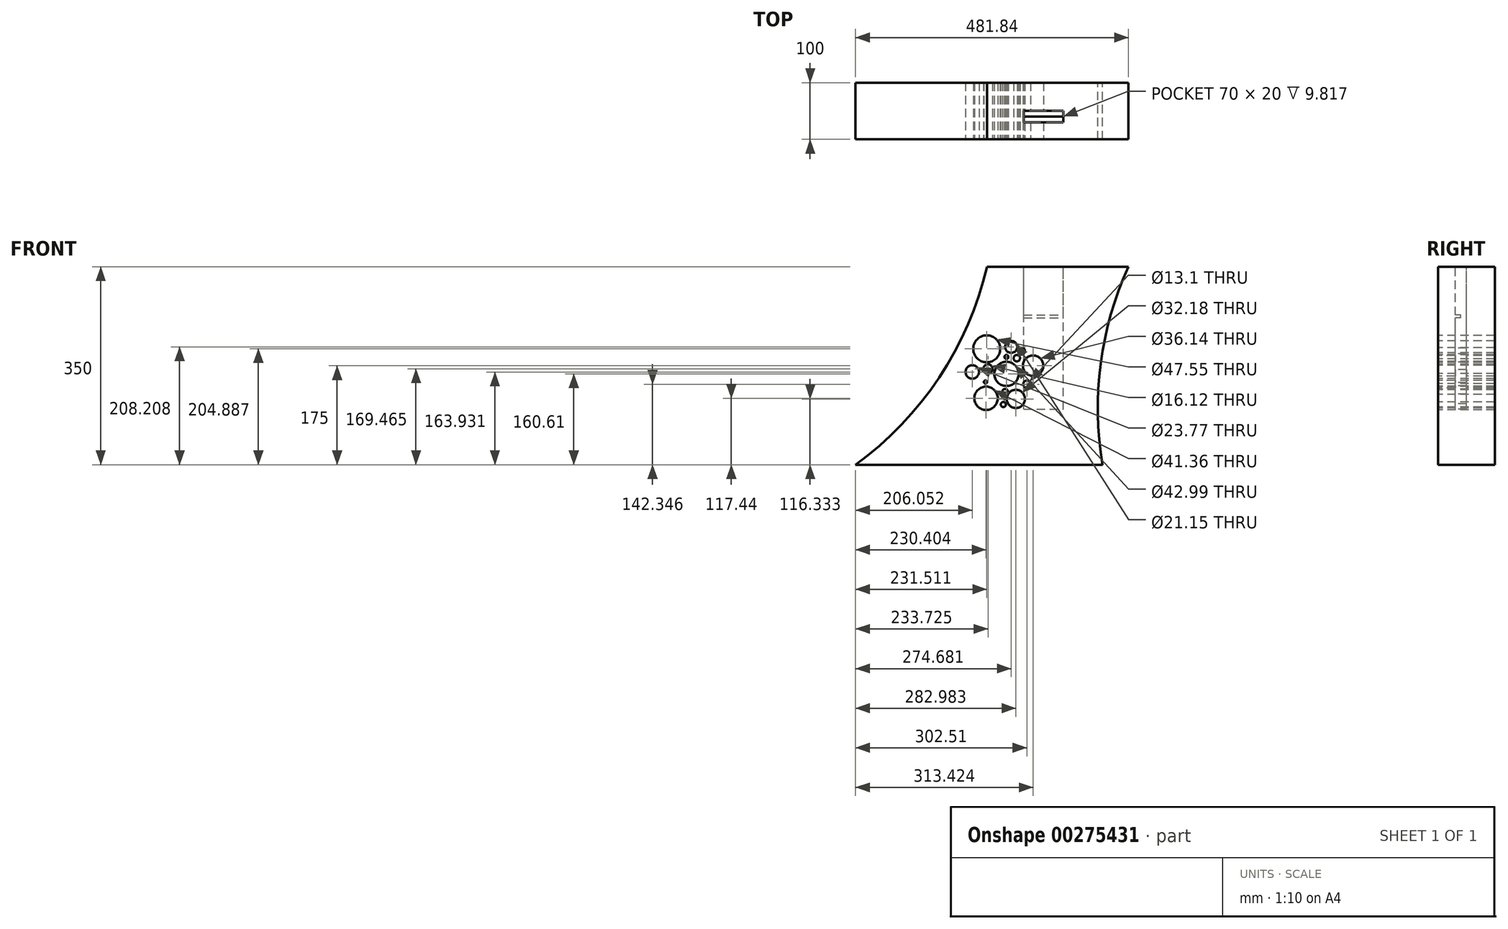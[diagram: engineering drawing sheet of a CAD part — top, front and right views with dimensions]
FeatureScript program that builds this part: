
annotation { "Feature Type Name" : "Feature", "Feature Type Description" : "" }
export const myFeature = defineFeature(function(context is Context, id is Id, definition is map)
    precondition{}
    {
        {
            var Q0;
            Q0=qCreatedBy(makeId("Front.planeOp"),FACE);
            var sketch = newSketch(context, id + "F0", { "sketchPlane" : qUnion([Q0])});
            skLineSegment(sketch, "E0.bottom", {"start": v(-70.67, 175) * mm, "end": v(179.33, 175) * mm});
            skLineSegment(sketch, "E0.top", {"start": v(-302.51, -175) * mm, "end": v(133.65, -175) * mm});
            skArc(sketch, "E1", {"start": v(-302.51, -175) * mm, "mid": v(-154.98, -20.94) * mm, "end": v(-70.67, 175) * mm});
            skArc(sketch, "E2", {"start": v(179.33, 175) * mm, "mid": v(130.17, 3.44) * mm, "end": v(133.65, -175) * mm});
            skSolve(sketch);
        }
        {
            var Q0;
            Q0=qSketchRegion(id+"F0",true);
            extrude(context, id + "F1", {"entities" : qUnion([Q0]), "depth" : 100 * mm});
        }
        {
            var Q0;
            Q0=makeQuery(id+"F1.opExtrude","SWEPT_FACE",FACE,{"disambiguationData":[OSD([sQuery(id+"F0.wireOp",EDGE,"E0.bottom")])]});
            var sketch = newSketch(context, id + "F2", { "sketchPlane" : qUnion([Q0])});
            skLineSegment(sketch, "E3.bottom", {"start": v(-5.88, -50) * mm, "end": v(64.12, -50) * mm});
            skLineSegment(sketch, "E3.top", {"start": v(-5.88, -70) * mm, "end": v(64.12, -70) * mm});
            skLineSegment(sketch, "E3.left", {"start": v(-5.88, -50) * mm, "end": v(-5.88, -70) * mm});
            skLineSegment(sketch, "E3.right", {"start": v(64.12, -50) * mm, "end": v(64.12, -70) * mm});
            skSolve(sketch);
        }
        {
            var Q0;
            Q0=qSketchRegion(id+"F2",true);
            extrude(context, id + "F3", {"entities" : qUnion([Q0]), "operationType" : NewBodyOperationType.REMOVE, "oppositeDirection" : true, "depth" : 252 * mm});
        }
        {
            var Q0;
            Q0=makeQuery(id+"F1.opExtrude","CAP_FACE",FACE,{"disambiguationData":[OSD([sQuery(id+"F0.wireOp",EDGE,"E0.bottom"),sQuery(id+"F0.wireOp",EDGE,"E0.top"),sQuery(id+"F0.wireOp",EDGE,"E1"),sQuery(id+"F0.wireOp",EDGE,"E2")])],"isStart":false});
            var sketch = newSketch(context, id + "F4", { "sketchPlane" : qUnion([Q0])});
            skLineSegment(sketch, "E4.bottom", {"start": v(-26.75, 89.5) * mm, "end": v(111.14, 89.5) * mm});
            skLineSegment(sketch, "E4.top", {"start": v(-26.75, 84.76) * mm, "end": v(111.14, 84.76) * mm});
            skLineSegment(sketch, "E4.left", {"start": v(-26.75, 89.5) * mm, "end": v(-26.75, 84.76) * mm});
            skLineSegment(sketch, "E4.right", {"start": v(111.14, 89.5) * mm, "end": v(111.14, 84.76) * mm});
            skSolve(sketch);
        }
        {
            var Q0;
            Q0 = qSketchRegion(id + "F4", true);
            extrude(context, id + "F5", {"entities" : qUnion([Q0]), "operationType" : NewBodyOperationType.ADD, "oppositeDirection" : true, "depth" : 40 * mm});
        }
        {
            var Q0;
            Q0=makeQuery(id+"F1.opExtrude","CAP_FACE",FACE,{"disambiguationData":[OSD([sQuery(id+"F0.wireOp",EDGE,"E0.bottom"),sQuery(id+"F0.wireOp",EDGE,"E0.top"),sQuery(id+"F0.wireOp",EDGE,"E1"),sQuery(id+"F0.wireOp",EDGE,"E2")])],"isStart":false});
            var sketch = newSketch(context, id + "F6", { "sketchPlane" : qUnion([Q0])});
            skCircle(sketch, "E5", {"center": v(-71, 29.89) * mm, "radius": 23.77 * mm});
            skCircle(sketch, "E6", {"center": v(-36.13, -14.4) * mm, "radius": 21.5 * mm});
            skCircle(sketch, "E7", {"center": v(-72.1, -57.56) * mm, "radius": 20.68 * mm});
            skCircle(sketch, "E8", {"center": v(-96.46, -11.07) * mm, "radius": 11.88 * mm});
            skCircle(sketch, "E9", {"center": v(0, -32.65) * mm, "radius": 6.55 * mm});
            skCircle(sketch, "E10", {"center": v(-19.53, -58.67) * mm, "radius": 16.09 * mm});
            skCircle(sketch, "E11", {"center": v(10.91, 0) * mm, "radius": 18.07 * mm});
            skCircle(sketch, "E12", {"center": v(-27.83, 33.2) * mm, "radius": 10.57 * mm});
            skCircle(sketch, "E13", {"center": v(-9.56, 26.01) * mm, "radius": 6.11 * mm});
            skCircle(sketch, "E14", {"center": v(-68.79, -5.53) * mm, "radius": 8.06 * mm});
            skCircle(sketch, "E15", {"center": v(-73.21, -28.78) * mm, "radius": 2.77 * mm});
            skCircle(sketch, "E16", {"center": v(-38.34, -45.94) * mm, "radius": 4.98 * mm});
            skCircle(sketch, "E17", {"center": v(-41.67, -68.63) * mm, "radius": 4.46 * mm});
            skCircle(sketch, "E18", {"center": v(-17.87, 13.28) * mm, "radius": 5.64 * mm});
            skCircle(sketch, "E19", {"center": v(-36.13, 15.5) * mm, "radius": 3.5 * mm});
            skSolve(sketch);
        }
        {
            var Q0;
            Q0 = qSketchRegion(id + "F6", true);
            extrude(context, id + "F7", {"entities" : qUnion([Q0]), "operationType" : NewBodyOperationType.REMOVE, "oppositeDirection" : true, "depth" : 357 * mm});
        }
    });
